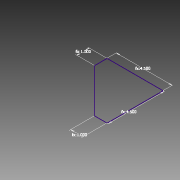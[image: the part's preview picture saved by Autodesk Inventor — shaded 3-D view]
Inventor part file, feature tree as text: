
AUTODESK INVENTOR PART (.ipt)
format: ipt  version: 2015 SP1 (Build 190203100, 203)  size: 95,744 bytes
history: native  units: in
note: dims shown in document units (in); Inventor stores cm internally (conversion verified against a paired STEP export)
features: other x1, sketch x1
ambient origin geometry x8: Origin, YZ Plane, XZ Plane, XY Plane, X Axis, Y Axis, Z Axis, Center Point
feature tree (2):
  other  "<userpath>\Documents\2015 Offseason Chassis\West Coast Chassis Fall 2015\rivet(rv).xlsx"
  sketch  "Sketch1"  dims[d0=4.5in d1=4.5in d2=1.0in d3=1.0in]
